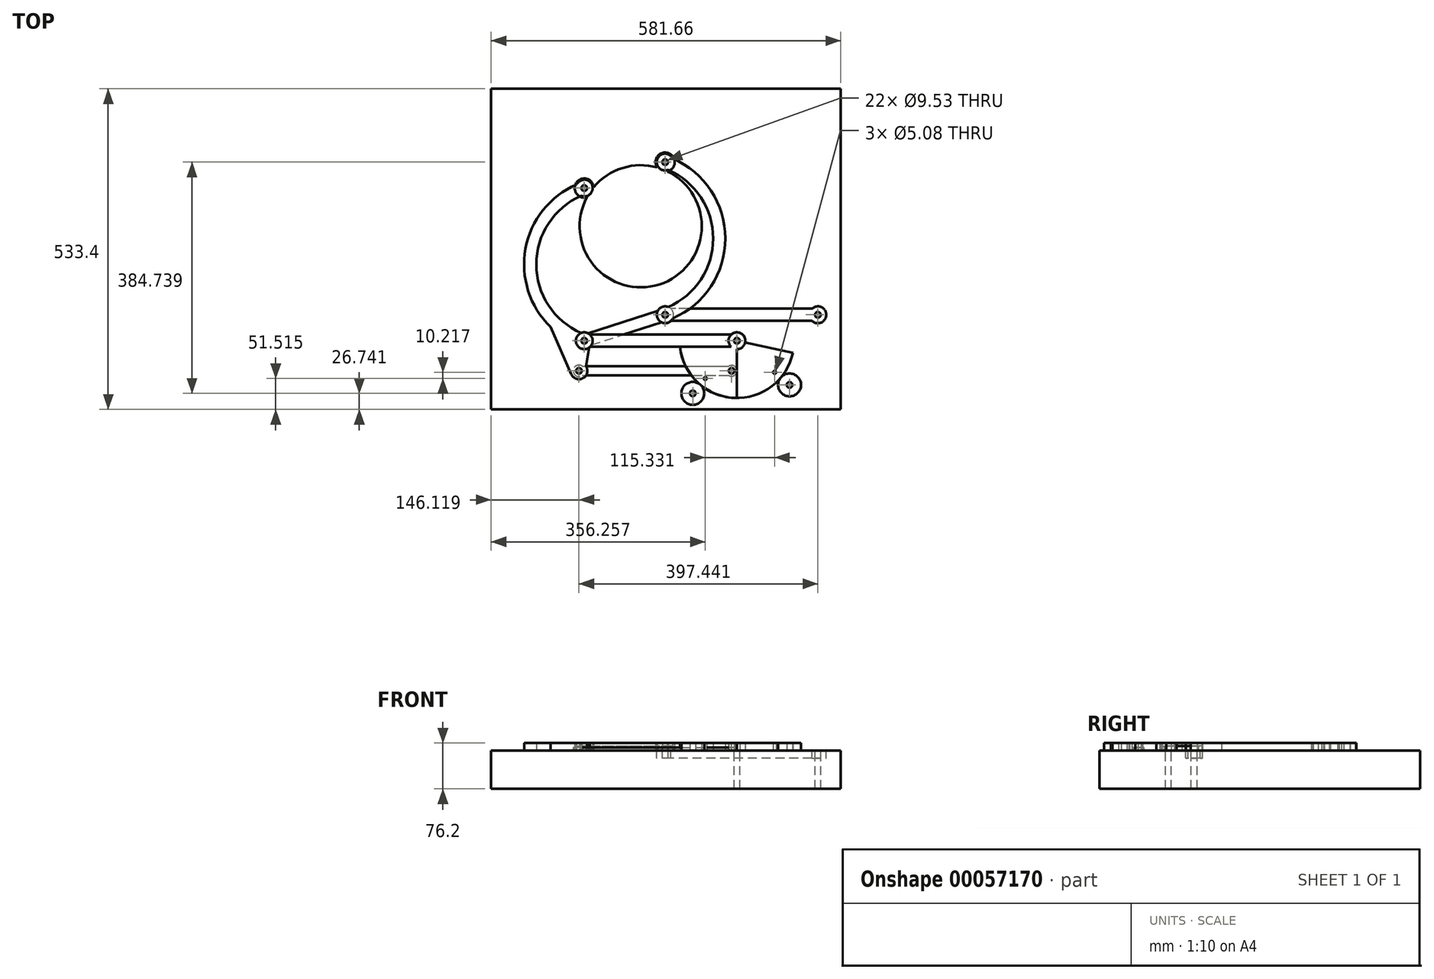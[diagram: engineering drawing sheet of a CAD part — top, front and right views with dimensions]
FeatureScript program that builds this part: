
annotation { "Feature Type Name" : "Feature", "Feature Type Description" : "" }
export const myFeature = defineFeature(function(context is Context, id is Id, definition is map)
    precondition{}
    {
        {
            var Q0;
            Q0=qCreatedBy(makeId("Top.planeOp"),FACE);
            var sketch = newSketch(context, id + "F0", { "sketchPlane" : qUnion([Q0])});
            skCircle(sketch, "E0", {"center": v(0, 0) * mm, "radius": 203.2 * mm, "construction": true});
            skLineSegment(sketch, "E1.bottom", {"start": v(-248.92, 228.6) * mm, "end": v(332.74, 228.6) * mm});
            skLineSegment(sketch, "E1.top", {"start": v(-248.92, -304.8) * mm, "end": v(332.74, -304.8) * mm});
            skLineSegment(sketch, "E1.left", {"start": v(-248.92, 228.6) * mm, "end": v(-248.92, -304.8) * mm});
            skLineSegment(sketch, "E1.right", {"start": v(332.74, 228.6) * mm, "end": v(332.74, -304.8) * mm});
            skLineSegment(sketch, "E2", {"start": v(0, 0) * mm, "end": v(168.4, 0) * mm, "construction": true});
            skLineSegment(sketch, "E3", {"start": v(0, 0) * mm, "end": v(0, 160.64) * mm, "construction": true});
            skLineSegment(sketch, "E4", {"start": v(-93.98, 63.5) * mm, "end": v(-93.98, -190.5) * mm, "construction": true});
            skLineSegment(sketch, "E5", {"start": v(-93.98, -190.5) * mm, "end": v(160.02, -190.5) * mm, "construction": true});
            skArc(sketch, "E6", {"start": v(-72.91, -89.22) * mm, "mid": v(-93.98, -190.85) * mm, "end": v(-72.64, -292.42) * mm, "construction": true});
            skArc(sketch, "E7", {"start": v(7.3, 42.43) * mm, "mid": v(-94.33, 63.5) * mm, "end": v(-195.9, 42.16) * mm, "construction": true});
            skLineSegment(sketch, "E8", {"start": v(-195.9, 42.16) * mm, "end": v(7.3, 42.43) * mm, "construction": true});
            skLineSegment(sketch, "E9", {"start": v(-72.91, -89.22) * mm, "end": v(-72.64, -292.42) * mm, "construction": true});
            skLineSegment(sketch, "E10", {"start": v(160.02, -190.5) * mm, "end": v(-72.91, -89.22) * mm, "construction": true});
            skLineSegment(sketch, "E11", {"start": v(160.02, -190.5) * mm, "end": v(-72.64, -292.42) * mm, "construction": true});
            skLineSegment(sketch, "E12", {"start": v(-195.9, 42.16) * mm, "end": v(-93.98, -190.5) * mm, "construction": true});
            skLineSegment(sketch, "E13", {"start": v(7.3, 42.43) * mm, "end": v(-93.98, -190.5) * mm, "construction": true});
            skCircle(sketch, "E14", {"center": v(0, 0) * mm, "radius": 101.6 * mm});
            skCircle(sketch, "E15", {"center": v(0, 0) * mm, "radius": 100 * mm, "construction": true});
            skCircle(sketch, "E16", {"center": v(-100, 0) * mm, "radius": 100 * mm, "construction": true});
            skCircle(sketch, "E17", {"center": v(100, 0) * mm, "radius": 100 * mm, "construction": true});
            skCircle(sketch, "E18", {"center": v(0, -100) * mm, "radius": 100 * mm, "construction": true});
            skCircle(sketch, "E19", {"center": v(0, 100) * mm, "radius": 100 * mm, "construction": true});
            skCircle(sketch, "E20", {"center": v(-93.98, 63.5) * mm, "radius": 15.88 * mm});
            skCircle(sketch, "E21", {"center": v(-93.98, 63.5) * mm, "radius": 4.76 * mm});
            skArc(sketch, "E22", {"start": v(-93.98, 63.5) * mm, "mid": v(-183.95, -63.5) * mm, "end": v(-93.98, -190.5) * mm, "construction": true});
            skPoint(sketch, "E23", {"position": v(-193.98, 63.5) * mm});
            skLineSegment(sketch, "E24", {"start": v(-93.98, 63.5) * mm, "end": v(0, 0) * mm, "construction": true});
            skLineSegment(sketch, "E25", {"start": v(-193.98, 63.5) * mm, "end": v(-100, 0) * mm, "construction": true});
            skLineSegment(sketch, "E26", {"start": v(-193.98, 63.5) * mm, "end": v(-93.12, -169.62) * mm, "construction": true});
            skArc(sketch, "E27", {"start": v(-193.98, 63.5) * mm, "mid": v(-226.12, -88.78) * mm, "end": v(-93.12, -169.62) * mm, "construction": true});
            skPoint(sketch, "E28", {"position": v(-93.98, 163.5) * mm});
            skLineSegment(sketch, "E29", {"start": v(-93.98, 163.5) * mm, "end": v(0, 100) * mm, "construction": true});
            skLineSegment(sketch, "E30", {"start": v(-93.98, 163.5) * mm, "end": v(-73.1, -89.64) * mm, "construction": true});
            skArc(sketch, "E31", {"start": v(-93.98, 163.5) * mm, "mid": v(-173.2, 29.53) * mm, "end": v(-73.1, -89.64) * mm, "construction": true});
            skPoint(sketch, "E32", {"position": v(40.64, 106.68) * mm});
            skLineSegment(sketch, "E33", {"start": v(40.64, 106.68) * mm, "end": v(40.64, -147.32) * mm, "construction": true});
            skLineSegment(sketch, "E34", {"start": v(40.64, -147.32) * mm, "end": v(294.64, -147.32) * mm, "construction": true});
            skLineSegment(sketch, "E35", {"start": v(40.64, 106.68) * mm, "end": v(0, 0) * mm, "construction": true});
            skCircle(sketch, "E36", {"center": v(40.64, 106.68) * mm, "radius": 15.88 * mm});
            skCircle(sketch, "E37", {"center": v(40.64, 106.68) * mm, "radius": 4.76 * mm});
            skArc(sketch, "E38", {"start": v(40.64, -147.32) * mm, "mid": v(130.61, -20.32) * mm, "end": v(40.64, 106.68) * mm, "construction": true});
            skCircle(sketch, "E39", {"center": v(160.02, -190.5) * mm, "radius": 4.76 * mm});
            skCircle(sketch, "E40", {"center": v(294.64, -147.32) * mm, "radius": 4.76 * mm});
            skLineSegment(sketch, "E41", {"start": v(40.64, -147.32) * mm, "end": v(-93.98, -190.5) * mm, "construction": true});
            skSolve(sketch);
        }
        {
            var Q0;
            Q0=makeQuery(id+"F0.imprint","IMPRINT",FACE,{"disambiguationData":[TD([[makeQuery(id+"F0.imprint","IMPRINT",EDGE,{"derivedFrom":sQuery(id+"F0.wireOp",EDGE,"E1.bottom")}),-1.0]])]});
            var Q1;
            Q1=makeQuery(id+"F0.imprint","IMPRINT",FACE,{"disambiguationData":[TD([[makeQuery(id+"F0.imprint","IMPRINT",EDGE,{"derivedFrom":sQuery(id+"F0.wireOp",EDGE,"E37")}),-1.0]])]});
            var Q2;
            {var subQ0=sQuery(id+"F0.wireOp",EDGE,"E36");var subQ1=sQuery(id+"F0.wireOp",EDGE,"E14");var subQ3=makeQuery(id+"F0.imprint","INTERSECT",VERTEX,{"disambiguationData":[OD(0.0)],"derivedFrom":[subQ1,subQ0]});Q2=makeQuery(id+"F0.imprint","IMPRINT",FACE,{"disambiguationData":[TD([[makeQuery(id+"F0.imprint","IMPRINT",EDGE,{"disambiguationData":[TD([[subQ3,-1.0]])],"derivedFrom":subQ1}),1.0]])]});}
            var Q3;
            {var subQ0=sQuery(id+"F0.wireOp",EDGE,"E36");var subQ1=sQuery(id+"F0.wireOp",EDGE,"E14");var subQ3=makeQuery(id+"F0.imprint","INTERSECT",VERTEX,{"disambiguationData":[OD(0.0)],"derivedFrom":[subQ1,subQ0]});Q3=makeQuery(id+"F0.imprint","IMPRINT",FACE,{"disambiguationData":[TD([[makeQuery(id+"F0.imprint","IMPRINT",EDGE,{"disambiguationData":[TD([[subQ3,1.0]])],"derivedFrom":subQ1}),1.0]])]});}
            var Q4;
            Q4=makeQuery(id+"F0.imprint","IMPRINT",FACE,{"disambiguationData":[TD([[makeQuery(id+"F0.imprint","IMPRINT",EDGE,{"derivedFrom":sQuery(id+"F0.wireOp",EDGE,"E21")}),-1.0]])]});
            var Q5;
            {var subQ0=sQuery(id+"F0.wireOp",EDGE,"E20");var subQ1=sQuery(id+"F0.wireOp",EDGE,"E14");var subQ3=makeQuery(id+"F0.imprint","INTERSECT",VERTEX,{"disambiguationData":[OD(0.0)],"derivedFrom":[subQ1,subQ0]});Q5=makeQuery(id+"F0.imprint","IMPRINT",FACE,{"disambiguationData":[TD([[makeQuery(id+"F0.imprint","IMPRINT",EDGE,{"disambiguationData":[TD([[subQ3,-1.0]])],"derivedFrom":subQ1}),1.0]])]});}
            var Q6;
            Q6=makeQuery(id+"F0.imprint","IMPRINT",FACE,{"disambiguationData":[TD([[makeQuery(id+"F0.imprint","IMPRINT",EDGE,{"derivedFrom":sQuery(id+"F0.wireOp",EDGE,"E37")}),1.0]])]});
            var Q7;
            Q7=makeQuery(id+"F0.imprint","IMPRINT",FACE,{"disambiguationData":[TD([[makeQuery(id+"F0.imprint","IMPRINT",EDGE,{"derivedFrom":sQuery(id+"F0.wireOp",EDGE,"E21")}),1.0]])]});
            extrude(context, id + "F1", {"entities" : qUnion([Q0, Q1, Q2, Q3, Q4, Q5, Q6, Q7]), "oppositeDirection" : true, "depth" : 63.5 * mm});
        }
        {
            var Q0;
            {var subQ0=sQuery(id+"F0.wireOp",EDGE,"E36");var subQ1=sQuery(id+"F0.wireOp",EDGE,"E14");var subQ3=makeQuery(id+"F0.imprint","INTERSECT",VERTEX,{"disambiguationData":[OD(0.0)],"derivedFrom":[subQ1,subQ0]});Q0=makeQuery(id+"F0.imprint","IMPRINT",FACE,{"disambiguationData":[TD([[makeQuery(id+"F0.imprint","IMPRINT",EDGE,{"disambiguationData":[TD([[subQ3,-1.0]])],"derivedFrom":subQ1}),1.0]])]});}
            var Q1;
            Q1=makeQuery(id+"F0.imprint","IMPRINT",FACE,{"disambiguationData":[TD([[makeQuery(id+"F0.imprint","IMPRINT",EDGE,{"derivedFrom":sQuery(id+"F0.wireOp",EDGE,"E37")}),-1.0]])]});
            var Q2;
            {var subQ0=sQuery(id+"F0.wireOp",EDGE,"E36");var subQ1=sQuery(id+"F0.wireOp",EDGE,"E14");var subQ3=makeQuery(id+"F0.imprint","INTERSECT",VERTEX,{"disambiguationData":[OD(0.0)],"derivedFrom":[subQ1,subQ0]});Q2=makeQuery(id+"F0.imprint","IMPRINT",FACE,{"disambiguationData":[TD([[makeQuery(id+"F0.imprint","IMPRINT",EDGE,{"disambiguationData":[TD([[subQ3,1.0]])],"derivedFrom":subQ1}),1.0]])]});}
            var Q3;
            {var subQ0=sQuery(id+"F0.wireOp",EDGE,"E20");var subQ1=sQuery(id+"F0.wireOp",EDGE,"E14");var subQ3=makeQuery(id+"F0.imprint","INTERSECT",VERTEX,{"disambiguationData":[OD(0.0)],"derivedFrom":[subQ1,subQ0]});Q3=makeQuery(id+"F0.imprint","IMPRINT",FACE,{"disambiguationData":[TD([[makeQuery(id+"F0.imprint","IMPRINT",EDGE,{"disambiguationData":[TD([[subQ3,-1.0]])],"derivedFrom":subQ1}),1.0]])]});}
            var Q4;
            Q4=makeQuery(id+"F0.imprint","IMPRINT",FACE,{"disambiguationData":[TD([[makeQuery(id+"F0.imprint","IMPRINT",EDGE,{"derivedFrom":sQuery(id+"F0.wireOp",EDGE,"E21")}),-1.0]])]});
            extrude(context, id + "F2", {"entities" : qUnion([Q0, Q1, Q2, Q3, Q4]), "depth" : 12.7 * mm});
        }
        {
            var Q0;
            Q0=qCreatedBy(makeId("Top.planeOp"),FACE);
            var sketch = newSketch(context, id + "F3", { "sketchPlane" : qUnion([Q0])});
            skLineSegment(sketch, "E42", {"start": v(160.02, -190.5) * mm, "end": v(-93.98, -190.5) * mm, "construction": true});
            skLineSegment(sketch, "E43", {"start": v(294.64, -147.32) * mm, "end": v(40.64, -147.32) * mm, "construction": true});
            skLineSegment(sketch, "E44", {"start": v(-93.98, -190.5) * mm, "end": v(40.64, -147.32) * mm, "construction": true});
            skArc(sketch, "E45", {"start": v(40.64, -147.32) * mm, "mid": v(130.61, -20.32) * mm, "end": v(40.64, 106.68) * mm, "construction": true});
            skArc(sketch, "E46", {"start": v(-93.98, 63.5) * mm, "mid": v(-183.95, -63.5) * mm, "end": v(-93.98, -190.5) * mm, "construction": true});
            skCircle(sketch, "E47", {"center": v(40.64, -147.32) * mm, "radius": 13.97 * mm});
            skCircle(sketch, "E48", {"center": v(40.64, 106.68) * mm, "radius": 13.97 * mm});
            skCircle(sketch, "E49", {"center": v(294.64, -147.32) * mm, "radius": 13.97 * mm});
            skCircle(sketch, "E50", {"center": v(160.02, -190.5) * mm, "radius": 13.97 * mm});
            skCircle(sketch, "E51", {"center": v(-93.98, -190.5) * mm, "radius": 13.97 * mm});
            skCircle(sketch, "E52", {"center": v(-93.98, 63.5) * mm, "radius": 13.97 * mm});
            skCircle(sketch, "E53", {"center": v(294.64, -147.32) * mm, "radius": 4.76 * mm});
            skCircle(sketch, "E54", {"center": v(160.02, -190.5) * mm, "radius": 4.76 * mm});
            skCircle(sketch, "E55", {"center": v(40.64, -147.32) * mm, "radius": 4.76 * mm});
            skCircle(sketch, "E56", {"center": v(-93.98, -190.5) * mm, "radius": 4.76 * mm});
            skCircle(sketch, "E57", {"center": v(40.64, 106.68) * mm, "radius": 4.76 * mm});
            skCircle(sketch, "E58", {"center": v(-93.98, 63.5) * mm, "radius": 4.76 * mm});
            skArc(sketch, "E59.0", {"start": v(53.27, -153.29) * mm, "mid": v(140.77, -20.32) * mm, "end": v(53.27, 112.65) * mm});
            skArc(sketch, "E60.0", {"start": v(-99.19, 50.54) * mm, "mid": v(-173.8, -63.5) * mm, "end": v(-99.19, -177.54) * mm});
            skLineSegment(sketch, "E61.0", {"start": v(285.05, -137.16) * mm, "end": v(50.23, -137.16) * mm});
            skLineSegment(sketch, "E62.0", {"start": v(150.43, -180.34) * mm, "end": v(-84.4, -180.34) * mm});
            skLineSegment(sketch, "E63.0", {"start": v(285.05, -157.48) * mm, "end": v(50.23, -157.48) * mm});
            skLineSegment(sketch, "E64.0", {"start": v(150.43, -200.66) * mm, "end": v(-84.4, -200.66) * mm});
            skArc(sketch, "E65.0", {"start": v(-106.61, 69.47) * mm, "mid": v(-194.11, -63.5) * mm, "end": v(-106.61, -196.47) * mm});
            skArc(sketch, "E66.0", {"start": v(45.85, -134.36) * mm, "mid": v(120.45, -20.32) * mm, "end": v(45.85, 93.72) * mm});
            skLineSegment(sketch, "E67.0", {"start": v(-81.75, -197.25) * mm, "end": v(34.61, -159.92) * mm});
            skLineSegment(sketch, "E68.0", {"start": v(-87.95, -177.9) * mm, "end": v(28.4, -140.57) * mm});
            skArc(sketch, "E69", {"start": v(65.31, -200.66) * mm, "mid": v(155.14, -285.62) * mm, "end": v(253.19, -210.3) * mm});
            skLineSegment(sketch, "E70", {"start": v(86.55, -278.06) * mm, "end": v(160.02, -190.5) * mm, "construction": true});
            skCircle(sketch, "E71", {"center": v(86.55, -278.06) * mm, "radius": 19.05 * mm});
            skLineSegment(sketch, "E72", {"start": v(160.02, -285.75) * mm, "end": v(160.02, -190.5) * mm});
            skPoint(sketch, "E73", {"position": v(-102.8, -240.53) * mm});
            skLineSegment(sketch, "E74", {"start": v(-102.8, -240.53) * mm, "end": v(-93.98, -190.5) * mm, "construction": true});
            skCircle(sketch, "E75", {"center": v(-102.8, -240.53) * mm, "radius": 4.76 * mm});
            skCircle(sketch, "E76", {"center": v(-102.8, -240.53) * mm, "radius": 13.97 * mm});
            skLineSegment(sketch, "E77", {"start": v(-115.6, -246.15) * mm, "end": v(-150.2, -167.36) * mm});
            skLineSegment(sketch, "E78.0", {"start": v(-91.13, -232.85) * mm, "end": v(-85.64, -201.7) * mm});
            skLineSegment(sketch, "E79", {"start": v(160.02, -190.5) * mm, "end": v(151.2, -240.53) * mm, "construction": true});
            skLineSegment(sketch, "E80", {"start": v(151.2, -240.53) * mm, "end": v(-102.8, -240.53) * mm, "construction": true});
            skCircle(sketch, "E81", {"center": v(151.2, -240.53) * mm, "radius": 4.76 * mm});
            skCircle(sketch, "E82", {"center": v(247.58, -263.97) * mm, "radius": 19.05 * mm});
            skLineSegment(sketch, "E83", {"start": v(160.02, -190.5) * mm, "end": v(247.58, -263.97) * mm, "construction": true});
            skLineSegment(sketch, "E84", {"start": v(160.02, -190.5) * mm, "end": v(253.19, -210.3) * mm});
            skCircle(sketch, "E85", {"center": v(86.55, -278.06) * mm, "radius": 4.76 * mm});
            skCircle(sketch, "E86", {"center": v(107.34, -253.28) * mm, "radius": 2.54 * mm});
            skCircle(sketch, "E87", {"center": v(247.58, -263.97) * mm, "radius": 4.76 * mm});
            skCircle(sketch, "E88", {"center": v(222.67, -243.07) * mm, "radius": 2.54 * mm});
            skSolve(sketch);
        }
        {
            var Q0;
            {var subQ2=sQuery(id+"F3.wireOp",EDGE,"E77");Q0=makeQuery(id+"F3.imprint","IMPRINT",FACE,{"disambiguationData":[TD([[makeQuery(id+"F3.imprint","IMPRINT",EDGE,{"derivedFrom":subQ2}),-1.0]])]});}
            var Q1;
            Q1=makeQuery(id+"F3.imprint","IMPRINT",FACE,{"disambiguationData":[TD([[makeQuery(id+"F3.imprint","IMPRINT",EDGE,{"derivedFrom":sQuery(id+"F3.wireOp",EDGE,"E75")}),-1.0]])]});
            var Q2;
            {var subQ6=sQuery(id+"F3.wireOp",EDGE,"E60.0");Q2=makeQuery(id+"F3.imprint","IMPRINT",FACE,{"disambiguationData":[TD([[makeQuery(id+"F3.imprint","IMPRINT",EDGE,{"derivedFrom":subQ6}),-1.0]])]});}
            var Q3;
            Q3=makeQuery(id+"F3.imprint","IMPRINT",FACE,{"disambiguationData":[TD([[makeQuery(id+"F3.imprint","IMPRINT",EDGE,{"derivedFrom":sQuery(id+"F3.wireOp",EDGE,"E56")}),-1.0]])]});
            var Q4;
            Q4=makeQuery(id+"F3.imprint","IMPRINT",FACE,{"disambiguationData":[TD([[makeQuery(id+"F3.imprint","IMPRINT",EDGE,{"derivedFrom":sQuery(id+"F3.wireOp",EDGE,"E58")}),-1.0]])]});
            var Q5;
            {var subQ0=sQuery(id+"F3.wireOp",EDGE,"E66.0");Q5=makeQuery(id+"F3.imprint","IMPRINT",FACE,{"disambiguationData":[TD([[makeQuery(id+"F3.imprint","IMPRINT",EDGE,{"derivedFrom":subQ0}),-1.0]])]});}
            var Q6;
            Q6=makeQuery(id+"F3.imprint","IMPRINT",FACE,{"disambiguationData":[TD([[makeQuery(id+"F3.imprint","IMPRINT",EDGE,{"derivedFrom":sQuery(id+"F3.wireOp",EDGE,"E57")}),-1.0]])]});
            var Q7;
            {var subQ1=sQuery(id+"F3.wireOp",EDGE,"E59.0");var subQ3=sQuery(id+"F3.wireOp",EDGE,"E47");var subQ5=makeQuery(id+"F3.imprint","INTERSECT",VERTEX,{"derivedFrom":[subQ3,subQ1]});Q7=makeQuery(id+"F3.imprint","IMPRINT",FACE,{"disambiguationData":[TD([[makeQuery(id+"F3.imprint","IMPRINT",EDGE,{"disambiguationData":[TD([[subQ5,-1.0]])],"derivedFrom":subQ3}),-1.0]])]});}
            var Q8;
            Q8=makeQuery(id+"F3.imprint","IMPRINT",FACE,{"disambiguationData":[TD([[makeQuery(id+"F3.imprint","IMPRINT",EDGE,{"derivedFrom":sQuery(id+"F3.wireOp",EDGE,"E55")}),-1.0]])]});
            extrude(context, id + "F4", {"entities" : qUnion([Q0, Q1, Q2, Q3, Q4, Q5, Q6, Q7, Q8]), "depth" : 12.7 * mm});
        }
        {
            var Q0;
            {var subQ0=sQuery(id+"F3.wireOp",EDGE,"E63.0");Q0=makeQuery(id+"F3.imprint","IMPRINT",FACE,{"disambiguationData":[TD([[makeQuery(id+"F3.imprint","IMPRINT",EDGE,{"derivedFrom":subQ0}),-1.0]])]});}
            var Q1;
            Q1=makeQuery(id+"F3.imprint","IMPRINT",FACE,{"disambiguationData":[TD([[makeQuery(id+"F3.imprint","IMPRINT",EDGE,{"derivedFrom":sQuery(id+"F3.wireOp",EDGE,"E53")}),-1.0]])]});
            var Q2;
            {var subQ1=sQuery(id+"F3.wireOp",EDGE,"E59.0");var subQ3=sQuery(id+"F3.wireOp",EDGE,"E47");var subQ5=makeQuery(id+"F3.imprint","INTERSECT",VERTEX,{"derivedFrom":[subQ3,subQ1]});Q2=makeQuery(id+"F3.imprint","IMPRINT",FACE,{"disambiguationData":[TD([[makeQuery(id+"F3.imprint","IMPRINT",EDGE,{"disambiguationData":[TD([[subQ5,-1.0]])],"derivedFrom":subQ3}),-1.0]])]});}
            var Q3;
            Q3=makeQuery(id+"F3.imprint","IMPRINT",FACE,{"disambiguationData":[TD([[makeQuery(id+"F3.imprint","IMPRINT",EDGE,{"derivedFrom":sQuery(id+"F3.wireOp",EDGE,"E55")}),-1.0]])]});
            extrude(context, id + "F5", {"entities" : qUnion([Q0, Q1, Q2, Q3]), "oppositeDirection" : true, "depth" : 12.7 * mm});
        }
        {
            var Q0;
            {var subQ1=sQuery(id+"F3.wireOp",EDGE,"E62.0");var subQ8=sQuery(id+"F3.wireOp",EDGE,"E50");var subQ10=makeQuery(id+"F3.imprint","INTERSECT",VERTEX,{"derivedFrom":[subQ8,subQ1]});Q0=makeQuery(id+"F3.imprint","IMPRINT",FACE,{"disambiguationData":[TD([[makeQuery(id+"F3.imprint","IMPRINT",EDGE,{"disambiguationData":[TD([[subQ10,-1.0]])],"derivedFrom":subQ8}),-1.0]])]});}
            var Q1;
            {var subQ1=sQuery(id+"F3.wireOp",EDGE,"E62.0");var subQ3=sQuery(id+"F3.wireOp",EDGE,"E51");var subQ5=makeQuery(id+"F3.imprint","INTERSECT",VERTEX,{"derivedFrom":[subQ3,subQ1]});Q1=makeQuery(id+"F3.imprint","IMPRINT",FACE,{"disambiguationData":[TD([[makeQuery(id+"F3.imprint","IMPRINT",EDGE,{"disambiguationData":[TD([[subQ5,1.0]])],"derivedFrom":subQ3}),-1.0]])]});}
            var Q2;
            Q2=makeQuery(id+"F3.imprint","IMPRINT",FACE,{"disambiguationData":[TD([[makeQuery(id+"F3.imprint","IMPRINT",EDGE,{"derivedFrom":sQuery(id+"F3.wireOp",EDGE,"E56")}),-1.0]])]});
            var Q3;
            {var subQ3=sQuery(id+"F3.wireOp",EDGE,"E50");var subQ8=makeQuery(id+"F3.imprint","INTERSECT",VERTEX,{"derivedFrom":[subQ3,sQuery(id+"F3.wireOp",EDGE,"E62.0")]});Q3=makeQuery(id+"F3.imprint","IMPRINT",FACE,{"disambiguationData":[TD([[makeQuery(id+"F3.imprint","IMPRINT",EDGE,{"disambiguationData":[TD([[subQ8,-1.0]])],"derivedFrom":subQ3}),1.0]])]});}
            var Q4;
            {var subQ0=sQuery(id+"F3.wireOp",EDGE,"E84");var subQ3=sQuery(id+"F3.wireOp",EDGE,"E50");var subQ4=makeQuery(id+"F3.imprint","INTERSECT",VERTEX,{"derivedFrom":[subQ3,subQ0]});Q4=makeQuery(id+"F3.imprint","IMPRINT",FACE,{"disambiguationData":[TD([[makeQuery(id+"F3.imprint","IMPRINT",EDGE,{"disambiguationData":[TD([[subQ4,1.0]])],"derivedFrom":subQ3}),1.0]])]});}
            var Q5;
            Q5=makeQuery(id+"F3.imprint","IMPRINT",FACE,{"disambiguationData":[TD([[makeQuery(id+"F3.imprint","IMPRINT",EDGE,{"derivedFrom":sQuery(id+"F3.wireOp",EDGE,"E81")}),-1.0]])]});
            extrude(context, id + "F6", {"entities" : qUnion([Q0, Q1, Q2, Q3, Q4, Q5]), "depth" : 12.7 * mm});
        }
        {
            var Q0;
            {var subQ0=sQuery(id+"F3.wireOp",EDGE,"E84");var subQ1=sQuery(id+"F3.wireOp",EDGE,"E50");var subQ2=makeQuery(id+"F3.imprint","INTERSECT",VERTEX,{"derivedFrom":[subQ1,subQ0]});Q0=makeQuery(id+"F3.imprint","IMPRINT",FACE,{"disambiguationData":[TD([[makeQuery(id+"F3.imprint","IMPRINT",EDGE,{"disambiguationData":[TD([[subQ2,1.0]])],"derivedFrom":subQ1}),-1.0]])]});}
            var Q1;
            Q1=makeQuery(id+"F3.imprint","IMPRINT",FACE,{"disambiguationData":[TD([[makeQuery(id+"F3.imprint","IMPRINT",EDGE,{"derivedFrom":sQuery(id+"F3.wireOp",EDGE,"E81")}),-1.0]])]});
            var Q2;
            {var subQ3=sQuery(id+"F3.wireOp",EDGE,"E50");var subQ8=makeQuery(id+"F3.imprint","INTERSECT",VERTEX,{"derivedFrom":[subQ3,sQuery(id+"F3.wireOp",EDGE,"E62.0")]});Q2=makeQuery(id+"F3.imprint","IMPRINT",FACE,{"disambiguationData":[TD([[makeQuery(id+"F3.imprint","IMPRINT",EDGE,{"disambiguationData":[TD([[subQ8,-1.0]])],"derivedFrom":subQ3}),1.0]])]});}
            var Q3;
            {var subQ0=sQuery(id+"F3.wireOp",EDGE,"E84");var subQ3=sQuery(id+"F3.wireOp",EDGE,"E50");var subQ4=makeQuery(id+"F3.imprint","INTERSECT",VERTEX,{"derivedFrom":[subQ3,subQ0]});Q3=makeQuery(id+"F3.imprint","IMPRINT",FACE,{"disambiguationData":[TD([[makeQuery(id+"F3.imprint","IMPRINT",EDGE,{"disambiguationData":[TD([[subQ4,1.0]])],"derivedFrom":subQ3}),1.0]])]});}
            extrude(context, id + "F7", {"entities" : qUnion([Q0, Q1, Q2, Q3]), "depth" : 12.7 * mm});
        }
        {
            var Q0;
            Q0=makeQuery(id+"F3.imprint","IMPRINT",FACE,{"disambiguationData":[TD([[makeQuery(id+"F3.imprint","IMPRINT",EDGE,{"derivedFrom":sQuery(id+"F3.wireOp",EDGE,"E71")}),1.0]])]});
            var Q1;
            Q1=makeQuery(id+"F3.imprint","IMPRINT",FACE,{"disambiguationData":[TD([[makeQuery(id+"F3.imprint","IMPRINT",EDGE,{"derivedFrom":sQuery(id+"F3.wireOp",EDGE,"E82")}),1.0]])]});
            extrude(context, id + "F8", {"entities" : qUnion([Q0, Q1]), "depth" : 12.7 * mm});
        }
        {
            var Q0;
            {var subQ0=sQuery(id+"F3.wireOp",EDGE,"E68.0");Q0=makeQuery(id+"F3.imprint","IMPRINT",FACE,{"disambiguationData":[TD([[makeQuery(id+"F3.imprint","IMPRINT",EDGE,{"derivedFrom":subQ0}),-1.0]])]});}
            var Q1;
            Q1=makeQuery(id+"F3.imprint","IMPRINT",FACE,{"disambiguationData":[TD([[makeQuery(id+"F3.imprint","IMPRINT",EDGE,{"derivedFrom":sQuery(id+"F3.wireOp",EDGE,"E55")}),-1.0]])]});
            var Q2;
            Q2=makeQuery(id+"F3.imprint","IMPRINT",FACE,{"disambiguationData":[TD([[makeQuery(id+"F3.imprint","IMPRINT",EDGE,{"derivedFrom":sQuery(id+"F3.wireOp",EDGE,"E56")}),-1.0]])]});
            var Q3;
            {var subQ1=sQuery(id+"F3.wireOp",EDGE,"E62.0");var subQ3=sQuery(id+"F3.wireOp",EDGE,"E51");var subQ5=makeQuery(id+"F3.imprint","INTERSECT",VERTEX,{"derivedFrom":[subQ3,subQ1]});Q3=makeQuery(id+"F3.imprint","IMPRINT",FACE,{"disambiguationData":[TD([[makeQuery(id+"F3.imprint","IMPRINT",EDGE,{"disambiguationData":[TD([[subQ5,1.0]])],"derivedFrom":subQ3}),-1.0]])]});}
            extrude(context, id + "F9", {"entities" : qUnion([Q0, Q1, Q2, Q3]), "depth" : 7.62 * mm});
        }
        {
            var Q0;
            Q0=qCreatedBy(makeId("Top.planeOp"),FACE);
            var sketch = newSketch(context, id + "F10", { "sketchPlane" : qUnion([Q0])});
            skCircle(sketch, "E89", {"center": v(-102.8, -240.53) * mm, "radius": 9.53 * mm});
            skCircle(sketch, "E90", {"center": v(151.2, -240.53) * mm, "radius": 8.94 * mm});
            skLineSegment(sketch, "E91", {"start": v(-97.09, -232.9) * mm, "end": v(146.52, -232.9) * mm});
            skLineSegment(sketch, "E92", {"start": v(-97.09, -248.15) * mm, "end": v(146.52, -248.15) * mm});
            skLineSegment(sketch, "E93", {"start": v(-102.8, -240.53) * mm, "end": v(151.2, -240.53) * mm, "construction": true});
            skCircle(sketch, "E94", {"center": v(-102.8, -240.53) * mm, "radius": 4.76 * mm});
            skCircle(sketch, "E95", {"center": v(151.2, -240.53) * mm, "radius": 4.76 * mm});
            skSolve(sketch);
        }
        {
            var Q0;
            Q0=makeQuery(id+"F10.imprint","IMPRINT",FACE,{"disambiguationData":[TD([[makeQuery(id+"F10.imprint","IMPRINT",EDGE,{"derivedFrom":sQuery(id+"F10.wireOp",EDGE,"E94")}),-1.0]])]});
            var Q1;
            {var subQ1=sQuery(id+"F10.wireOp",EDGE,"E91");Q1=makeQuery(id+"F10.imprint","IMPRINT",FACE,{"disambiguationData":[TD([[makeQuery(id+"F10.imprint","IMPRINT",EDGE,{"derivedFrom":subQ1}),-1.0]])]});}
            var Q2;
            Q2=makeQuery(id+"F10.imprint","IMPRINT",FACE,{"disambiguationData":[TD([[makeQuery(id+"F10.imprint","IMPRINT",EDGE,{"derivedFrom":sQuery(id+"F10.wireOp",EDGE,"E95")}),-1.0]])]});
            extrude(context, id + "F11", {"entities" : qUnion([Q0, Q1, Q2]), "depth" : 5.08 * mm});
        }
    });
